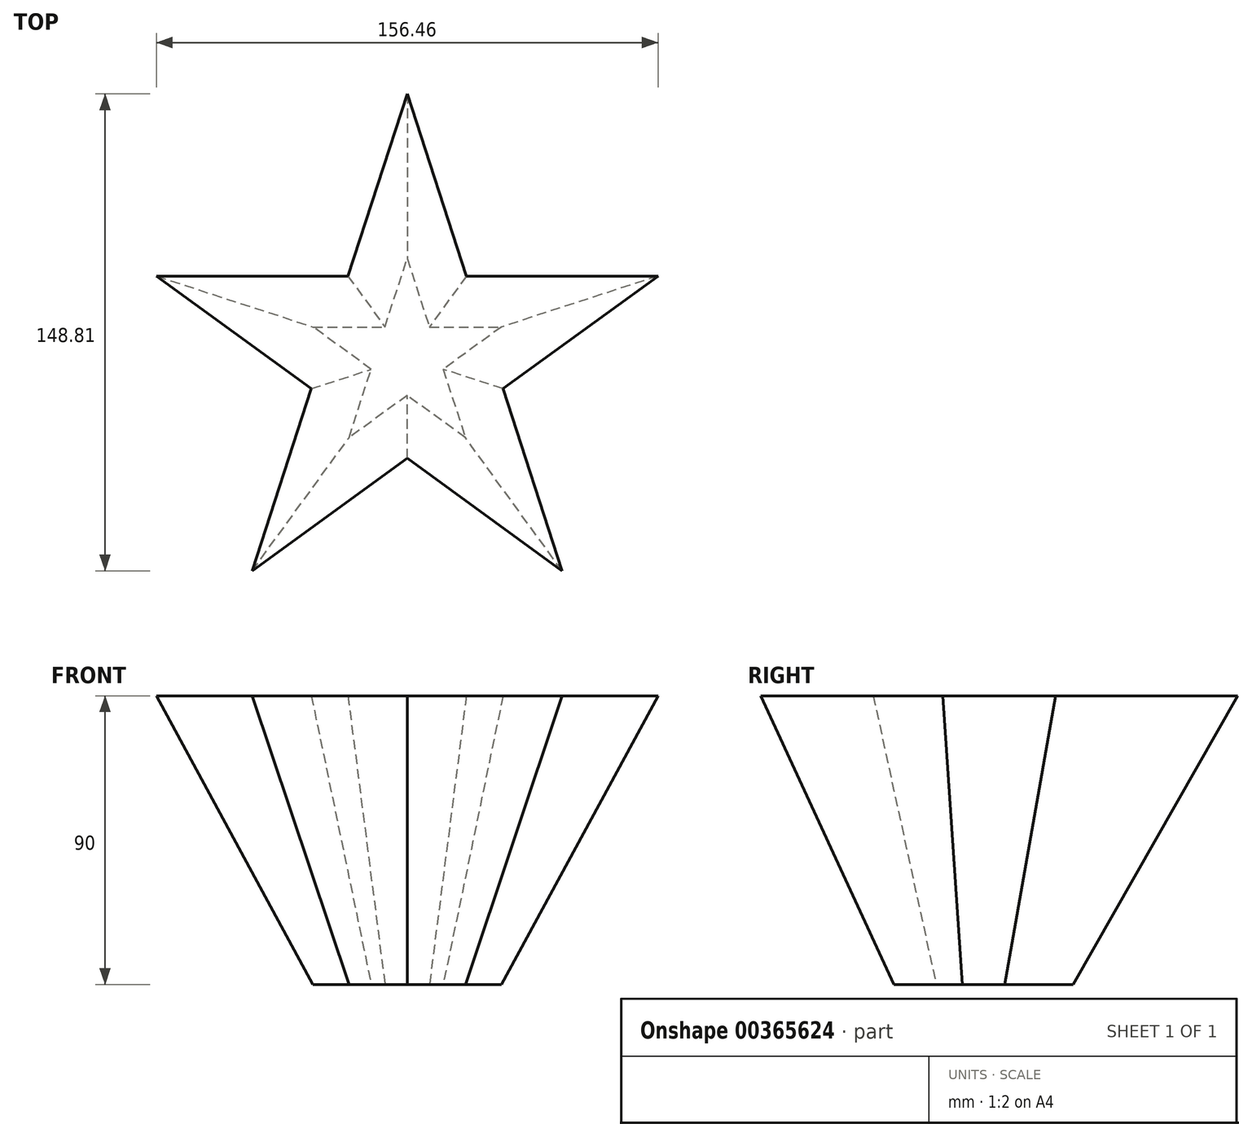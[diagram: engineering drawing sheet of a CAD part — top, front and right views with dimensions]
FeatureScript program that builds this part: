
annotation { "Feature Type Name" : "Feature", "Feature Type Description" : "" }
export const myFeature = defineFeature(function(context is Context, id is Id, definition is map)
    precondition{}
    {
        {
            var Q0;
            Q0=qCreatedBy(makeId("Top.planeOp"),FACE);
            var sketch = newSketch(context, id + "F0", { "sketchPlane" : qUnion([Q0])});
            skCircle(sketch, "E0.cCircle", {"center": v(0, 0) * mm, "radius": 25 * mm, "construction": true});
            skLineSegment(sketch, "E0.0", {"start": v(29.39, 9.55) * mm, "end": v(18.16, -25) * mm, "construction": true});
            skLineSegment(sketch, "E0.1", {"start": v(18.16, -25) * mm, "end": v(-18.16, -25) * mm, "construction": true});
            skLineSegment(sketch, "E0.2", {"start": v(-18.16, -25) * mm, "end": v(-29.39, 9.55) * mm, "construction": true});
            skLineSegment(sketch, "E0.3", {"start": v(-29.39, 9.55) * mm, "end": v(0, 30.9) * mm, "construction": true});
            skLineSegment(sketch, "E0.4", {"start": v(0, 30.9) * mm, "end": v(29.39, 9.55) * mm, "construction": true});
            skPoint(sketch, "E0.0.midPoint", {"position": v(23.78, -7.73) * mm});
            skLineSegment(sketch, "E1", {"start": v(-29.39, 9.55) * mm, "end": v(29.39, 9.55) * mm});
            skLineSegment(sketch, "E2", {"start": v(29.39, 9.55) * mm, "end": v(-18.16, -25) * mm});
            skLineSegment(sketch, "E3", {"start": v(-18.16, -25) * mm, "end": v(0, 30.9) * mm});
            skLineSegment(sketch, "E4", {"start": v(0, 30.9) * mm, "end": v(18.16, -25) * mm});
            skLineSegment(sketch, "E5", {"start": v(18.16, -25) * mm, "end": v(-29.39, 9.55) * mm});
            skSolve(sketch);
        }
        {
            var Q0;
            Q0=qCreatedBy(makeId("Top.planeOp"),FACE);
            cPlane(context, id + "F1", {"entities" : qUnion([Q0]), "cplaneType" : CPlaneType.OFFSET, "offset" : 90 * mm, "width" : 150 * mm, "height" : 150 * mm});
        }
        {
            var Q0;
            {var subQ0=sQuery(id+"F0.wireOp",EDGE,"E5");var subQ1=sQuery(id+"F0.wireOp",EDGE,"E1");var subQ2=makeQuery(id+"F0.imprint","INTERSECT",VERTEX,{"derivedFrom":[subQ1,subQ0]});Q0=makeQuery(id+"F0.imprint","IMPRINT",FACE,{"disambiguationData":[TD([[makeQuery(id+"F0.imprint","IMPRINT",EDGE,{"disambiguationData":[TD([[subQ2,-1.0]])],"derivedFrom":subQ1}),-1.0]])]});}
            var Q1;
            {var subQ0=sQuery(id+"F0.wireOp",EDGE,"E3");var subQ1=sQuery(id+"F0.wireOp",EDGE,"E2");var subQ2=makeQuery(id+"F0.imprint","INTERSECT",VERTEX,{"derivedFrom":[subQ1,subQ0]});Q1=makeQuery(id+"F0.imprint","IMPRINT",FACE,{"disambiguationData":[TD([[makeQuery(id+"F0.imprint","IMPRINT",EDGE,{"disambiguationData":[TD([[subQ2,1.0]])],"derivedFrom":subQ1}),-1.0]])]});}
            var Q2;
            {var subQ0=sQuery(id+"F0.wireOp",EDGE,"E4");var subQ1=sQuery(id+"F0.wireOp",EDGE,"E2");var subQ2=makeQuery(id+"F0.imprint","INTERSECT",VERTEX,{"derivedFrom":[subQ1,subQ0]});Q2=makeQuery(id+"F0.imprint","IMPRINT",FACE,{"disambiguationData":[TD([[makeQuery(id+"F0.imprint","IMPRINT",EDGE,{"disambiguationData":[TD([[subQ2,-1.0]])],"derivedFrom":subQ1}),1.0]])]});}
            var Q3;
            {var subQ1=sQuery(id+"F0.wireOp",EDGE,"E1");var subQ5=sQuery(id+"F0.wireOp",EDGE,"E3");var subQ6=makeQuery(id+"F0.imprint","INTERSECT",VERTEX,{"derivedFrom":[subQ1,subQ5]});Q3=makeQuery(id+"F0.imprint","IMPRINT",FACE,{"disambiguationData":[TD([[makeQuery(id+"F0.imprint","IMPRINT",EDGE,{"disambiguationData":[TD([[subQ6,-1.0]])],"derivedFrom":subQ1}),-1.0]])]});}
            var Q4;
            {var subQ0=sQuery(id+"F0.wireOp",EDGE,"E2");var subQ1=sQuery(id+"F0.wireOp",EDGE,"E1");var subQ2=makeQuery(id+"F0.imprint","INTERSECT",VERTEX,{"derivedFrom":[subQ1,subQ0]});Q4=makeQuery(id+"F0.imprint","IMPRINT",FACE,{"disambiguationData":[TD([[makeQuery(id+"F0.imprint","IMPRINT",EDGE,{"disambiguationData":[TD([[subQ2,1.0]])],"derivedFrom":subQ1}),-1.0]])]});}
            var Q5;
            {var subQ0=sQuery(id+"F0.wireOp",EDGE,"E3");var subQ1=sQuery(id+"F0.wireOp",EDGE,"E1");var subQ2=makeQuery(id+"F0.imprint","INTERSECT",VERTEX,{"derivedFrom":[subQ1,subQ0]});Q5=makeQuery(id+"F0.imprint","IMPRINT",FACE,{"disambiguationData":[TD([[makeQuery(id+"F0.imprint","IMPRINT",EDGE,{"disambiguationData":[TD([[subQ2,-1.0]])],"derivedFrom":subQ1}),1.0]])]});}
            extrude(context, id + "F2", {"entities" : qUnion([Q0, Q1, Q2, Q3, Q4, Q5]), "depth" : 90 * mm, "hasDraft" : true, "draftAngle" : 10 * degree});
        }
    });
